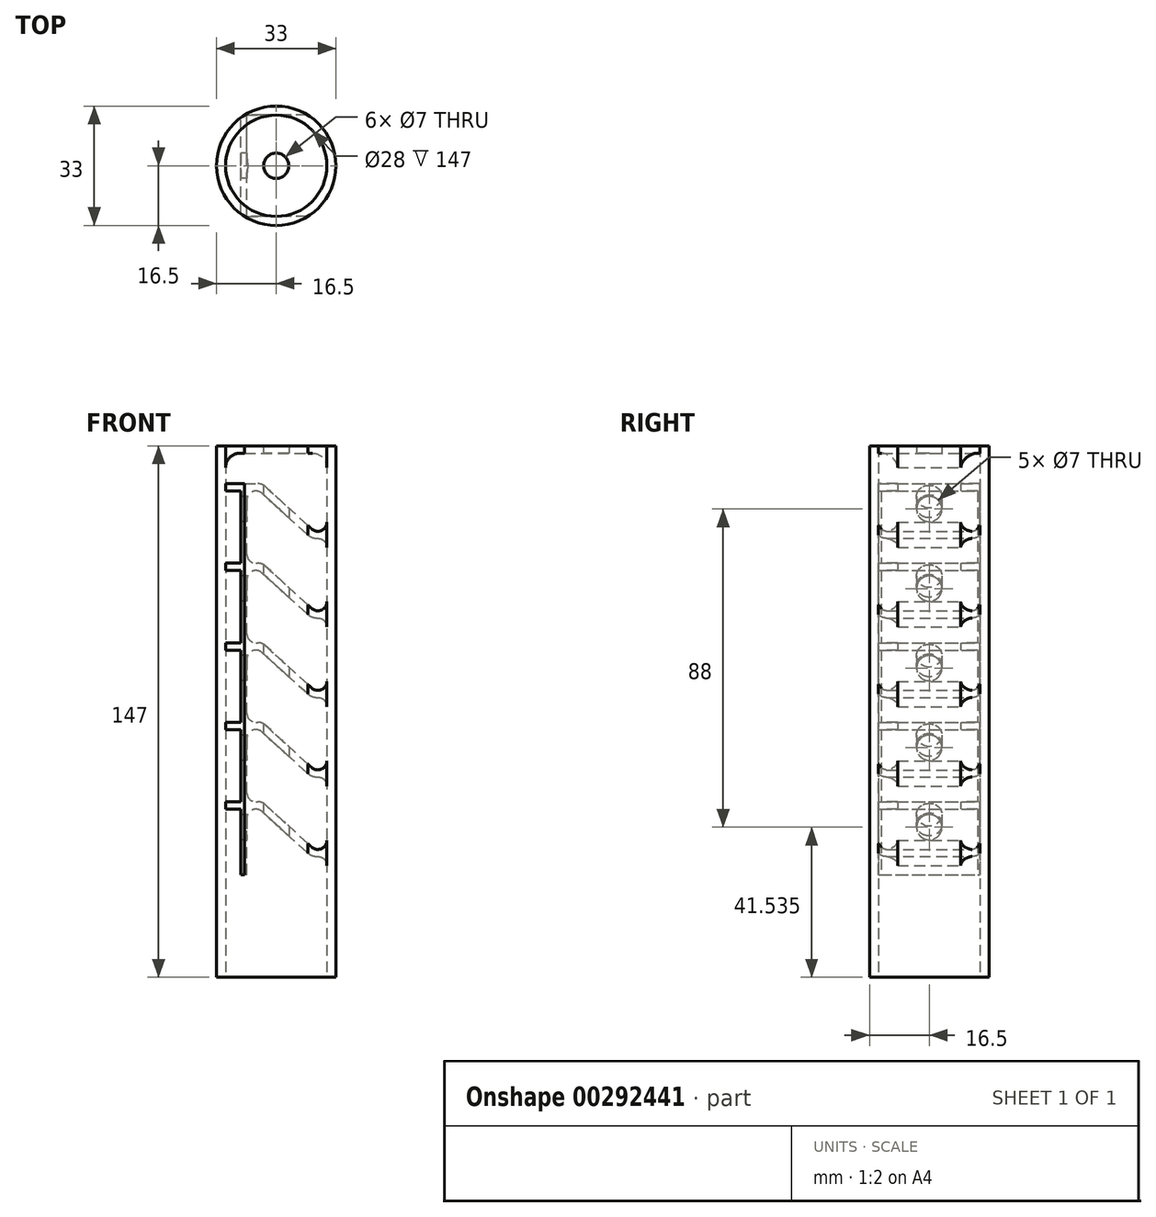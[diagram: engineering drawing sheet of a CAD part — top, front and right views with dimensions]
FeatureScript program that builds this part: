
annotation { "Feature Type Name" : "Feature", "Feature Type Description" : "" }
export const myFeature = defineFeature(function(context is Context, id is Id, definition is map)
    precondition{}
    {
        {
            var Q0;
            Q0=qCreatedBy(makeId("Front.planeOp"),FACE);
            var sketch = newSketch(context, id + "F0", { "sketchPlane" : qUnion([Q0])});
            skLineSegment(sketch, "E0.left", {"start": v(0, 0) * mm, "end": v(0, 125) * mm, "construction": true});
            skLineSegment(sketch, "E0.right", {"start": v(14, 0) * mm, "end": v(14, 125) * mm, "construction": true});
            skLineSegment(sketch, "E1.MirrorCS", {"start": v(-14, 0) * mm, "end": v(-14, 125) * mm, "construction": true});
            skLineSegment(sketch, "E2", {"start": v(-14, 125) * mm, "end": v(14, 125) * mm, "construction": true});
            skLineSegment(sketch, "E3", {"start": v(-3.5, 0) * mm, "end": v(-3.5, 125.09) * mm, "construction": true});
            skLineSegment(sketch, "E4", {"start": v(-9.71, 0) * mm, "end": v(-9.71, 34.88) * mm, "construction": true});
            skLineSegment(sketch, "E5", {"start": v(-3.5, 0) * mm, "end": v(-3.5, 73.23) * mm, "construction": true});
            skLineSegment(sketch, "E6.MirrorCS", {"start": v(3.5, 0) * mm, "end": v(3.5, 73.23) * mm, "construction": true});
            skLineSegment(sketch, "E7", {"start": v(-9.71, 36.85) * mm, "end": v(-9.71, 64.07) * mm, "construction": true});
            skCircle(sketch, "E8", {"center": v(11.5, 30.91) * mm, "radius": 2.5 * mm, "construction": true});
            skCircle(sketch, "E9", {"center": v(11.5, 37.89) * mm, "radius": 2.5 * mm, "construction": true});
            skCircle(sketch, "E10", {"center": v(-5.61, 44.03) * mm, "radius": 2.5 * mm, "construction": true});
            skCircle(sketch, "E11", {"center": v(-5.64, 51.03) * mm, "radius": 2.47 * mm, "construction": true});
            skLineSegment(sketch, "E12", {"start": v(-3.03, 47.77) * mm, "end": v(9.81, 36.04) * mm, "construction": true});
            skLineSegment(sketch, "E13", {"start": v(-4.64, 48.56) * mm, "end": v(-9.71, 48.56) * mm, "construction": true});
            skLineSegment(sketch, "E14", {"start": v(-5.61, 46.53) * mm, "end": v(-9.71, 46.53) * mm, "construction": true});
            skArc(sketch, "E15", {"start": v(14, 30.91) * mm, "mid": v(13.27, 32.68) * mm, "end": v(11.5, 33.41) * mm});
            skArc(sketch, "E16", {"start": v(14, 37.89) * mm, "mid": v(12.5, 35.6) * mm, "end": v(9.81, 36.04) * mm});
            skArc(sketch, "E17", {"start": v(-8.11, 51.03) * mm, "mid": v(-7.39, 49.28) * mm, "end": v(-5.64, 48.56) * mm});
            skArc(sketch, "E18", {"start": v(-8.11, 44.03) * mm, "mid": v(-6.62, 46.31) * mm, "end": v(-3.92, 45.87) * mm});
            skLineSegment(sketch, "E19", {"start": v(-9.71, 51.03) * mm, "end": v(-8.11, 51.03) * mm});
            skLineSegment(sketch, "E20", {"start": v(-14, 48.56) * mm, "end": v(-14, 46.53) * mm});
            skLineSegment(sketch, "E21", {"start": v(-14, 48.56) * mm, "end": v(-9.71, 48.56) * mm});
            skLineSegment(sketch, "E22", {"start": v(-9.71, 48.56) * mm, "end": v(-9.71, 51.03) * mm});
            skLineSegment(sketch, "E23", {"start": v(-14, 46.53) * mm, "end": v(-9.71, 46.53) * mm});
            skLineSegment(sketch, "E24", {"start": v(-8.11, 28.4) * mm, "end": v(-9.71, 28.41) * mm});
            skLineSegment(sketch, "E25", {"start": v(-5.64, 48.56) * mm, "end": v(-5.06, 48.56) * mm});
            skLineSegment(sketch, "E26", {"start": v(9.81, 36.04) * mm, "end": v(-3.9, 48.56) * mm});
            skLineSegment(sketch, "E27", {"start": v(14, 37.89) * mm, "end": v(14, 30.91) * mm});
            skLineSegment(sketch, "E28", {"start": v(-8.11, 28.4) * mm, "end": v(-8.11, 44.03) * mm});
            skLineSegment(sketch, "E29", {"start": v(-9.71, 46.53) * mm, "end": v(-9.71, 28.41) * mm});
            skPoint(sketch, "E30.visualSharp", {"position": v(-3.9, 48.56) * mm});
            skArc(sketch, "E30.filletArc", {"start": v(-3.03, 47.77) * mm, "mid": v(-3.97, 48.36) * mm, "end": v(-5.06, 48.56) * mm});
            skArc(sketch, "E31", {"start": v(11.5, 33.41) * mm, "mid": v(9.87, 33.72) * mm, "end": v(8.46, 34.6) * mm});
            skLineSegment(sketch, "E32", {"start": v(8.46, 34.6) * mm, "end": v(-3.92, 45.87) * mm});
            skLineSegment(sketch, "E33.0.1.0", {"start": v(-14, 70.56) * mm, "end": v(-9.71, 70.56) * mm});
            skLineSegment(sketch, "E33.0.1.1", {"start": v(-5.61, 68.53) * mm, "end": v(-9.71, 68.53) * mm, "construction": true});
            skLineSegment(sketch, "E33.0.1.2", {"start": v(-3.03, 69.77) * mm, "end": v(9.81, 58.04) * mm, "construction": true});
            skLineSegment(sketch, "E33.0.1.3", {"start": v(8.46, 56.6) * mm, "end": v(-3.92, 67.87) * mm});
            skLineSegment(sketch, "E33.0.1.4", {"start": v(-9.71, 68.53) * mm, "end": v(-9.71, 50.41) * mm});
            skPoint(sketch, "E33.0.1.5", {"position": v(-3.9, 70.56) * mm});
            skLineSegment(sketch, "E33.0.1.6", {"start": v(-8.11, 50.4) * mm, "end": v(-8.11, 66.03) * mm});
            skLineSegment(sketch, "E33.0.1.7", {"start": v(-4.64, 70.56) * mm, "end": v(-9.71, 70.56) * mm, "construction": true});
            skLineSegment(sketch, "E33.0.1.8", {"start": v(-14, 68.53) * mm, "end": v(-9.71, 68.53) * mm});
            skLineSegment(sketch, "E33.0.1.9", {"start": v(14, 59.89) * mm, "end": v(14, 52.91) * mm});
            skArc(sketch, "E33.0.1.10", {"start": v(-8.11, 66.03) * mm, "mid": v(-6.62, 68.31) * mm, "end": v(-3.92, 67.87) * mm});
            skLineSegment(sketch, "E33.0.1.11", {"start": v(9.81, 58.04) * mm, "end": v(-3.9, 70.56) * mm});
            skArc(sketch, "E33.0.1.12", {"start": v(14, 52.91) * mm, "mid": v(13.27, 54.68) * mm, "end": v(11.5, 55.41) * mm});
            skArc(sketch, "E33.0.1.13", {"start": v(14, 59.89) * mm, "mid": v(12.5, 57.6) * mm, "end": v(9.81, 58.04) * mm});
            skArc(sketch, "E33.0.1.14", {"start": v(-8.11, 73.03) * mm, "mid": v(-7.39, 71.28) * mm, "end": v(-5.64, 70.56) * mm});
            skArc(sketch, "E33.0.1.15", {"start": v(11.5, 55.41) * mm, "mid": v(9.87, 55.72) * mm, "end": v(8.46, 56.6) * mm});
            skLineSegment(sketch, "E33.0.1.16", {"start": v(-9.71, 70.56) * mm, "end": v(-9.71, 73.03) * mm});
            skLineSegment(sketch, "E33.0.1.17", {"start": v(-9.71, 73.03) * mm, "end": v(-8.11, 73.03) * mm});
            skLineSegment(sketch, "E33.0.1.18", {"start": v(-14, 70.56) * mm, "end": v(-14, 68.53) * mm});
            skLineSegment(sketch, "E33.0.1.19", {"start": v(-8.11, 50.4) * mm, "end": v(-9.71, 50.41) * mm});
            skArc(sketch, "E33.0.1.20", {"start": v(-3.03, 69.77) * mm, "mid": v(-3.97, 70.36) * mm, "end": v(-5.06, 70.56) * mm});
            skLineSegment(sketch, "E33.0.1.21", {"start": v(-5.64, 70.56) * mm, "end": v(-5.06, 70.56) * mm});
            skLineSegment(sketch, "E33.0.2.0", {"start": v(-14, 92.56) * mm, "end": v(-9.71, 92.56) * mm});
            skLineSegment(sketch, "E33.0.2.1", {"start": v(-5.61, 90.53) * mm, "end": v(-9.71, 90.53) * mm, "construction": true});
            skLineSegment(sketch, "E33.0.2.2", {"start": v(-3.03, 91.77) * mm, "end": v(9.81, 80.04) * mm, "construction": true});
            skLineSegment(sketch, "E33.0.2.3", {"start": v(8.46, 78.6) * mm, "end": v(-3.92, 89.87) * mm});
            skLineSegment(sketch, "E33.0.2.4", {"start": v(-9.71, 90.53) * mm, "end": v(-9.71, 72.41) * mm});
            skPoint(sketch, "E33.0.2.5", {"position": v(-3.9, 92.56) * mm});
            skLineSegment(sketch, "E33.0.2.6", {"start": v(-8.11, 72.4) * mm, "end": v(-8.11, 88.03) * mm});
            skLineSegment(sketch, "E33.0.2.7", {"start": v(-4.64, 92.56) * mm, "end": v(-9.71, 92.56) * mm, "construction": true});
            skLineSegment(sketch, "E33.0.2.8", {"start": v(-14, 90.53) * mm, "end": v(-9.71, 90.53) * mm});
            skLineSegment(sketch, "E33.0.2.9", {"start": v(14, 81.89) * mm, "end": v(14, 74.91) * mm});
            skArc(sketch, "E33.0.2.10", {"start": v(-8.11, 88.03) * mm, "mid": v(-6.62, 90.31) * mm, "end": v(-3.92, 89.87) * mm});
            skLineSegment(sketch, "E33.0.2.11", {"start": v(9.81, 80.04) * mm, "end": v(-3.9, 92.56) * mm});
            skArc(sketch, "E33.0.2.12", {"start": v(14, 74.91) * mm, "mid": v(13.27, 76.68) * mm, "end": v(11.5, 77.41) * mm});
            skArc(sketch, "E33.0.2.13", {"start": v(14, 81.89) * mm, "mid": v(12.5, 79.6) * mm, "end": v(9.81, 80.04) * mm});
            skArc(sketch, "E33.0.2.14", {"start": v(-8.11, 95.03) * mm, "mid": v(-7.39, 93.28) * mm, "end": v(-5.64, 92.56) * mm});
            skArc(sketch, "E33.0.2.15", {"start": v(11.5, 77.41) * mm, "mid": v(9.87, 77.72) * mm, "end": v(8.46, 78.6) * mm});
            skLineSegment(sketch, "E33.0.2.16", {"start": v(-9.71, 92.56) * mm, "end": v(-9.71, 95.03) * mm});
            skLineSegment(sketch, "E33.0.2.17", {"start": v(-9.71, 95.03) * mm, "end": v(-8.11, 95.03) * mm});
            skLineSegment(sketch, "E33.0.2.18", {"start": v(-14, 92.56) * mm, "end": v(-14, 90.53) * mm});
            skLineSegment(sketch, "E33.0.2.19", {"start": v(-8.11, 72.4) * mm, "end": v(-9.71, 72.41) * mm});
            skArc(sketch, "E33.0.2.20", {"start": v(-3.03, 91.77) * mm, "mid": v(-3.97, 92.36) * mm, "end": v(-5.06, 92.56) * mm});
            skLineSegment(sketch, "E33.0.2.21", {"start": v(-5.64, 92.56) * mm, "end": v(-5.06, 92.56) * mm});
            skLineSegment(sketch, "E33.0.3.0", {"start": v(-14, 114.56) * mm, "end": v(-9.71, 114.56) * mm});
            skLineSegment(sketch, "E33.0.3.1", {"start": v(-5.61, 112.53) * mm, "end": v(-9.71, 112.53) * mm, "construction": true});
            skLineSegment(sketch, "E33.0.3.2", {"start": v(-3.03, 113.77) * mm, "end": v(9.81, 102.04) * mm, "construction": true});
            skLineSegment(sketch, "E33.0.3.3", {"start": v(8.46, 100.6) * mm, "end": v(-3.92, 111.87) * mm});
            skLineSegment(sketch, "E33.0.3.4", {"start": v(-9.71, 112.53) * mm, "end": v(-9.71, 94.41) * mm});
            skPoint(sketch, "E33.0.3.5", {"position": v(-3.9, 114.56) * mm});
            skLineSegment(sketch, "E33.0.3.6", {"start": v(-8.11, 94.4) * mm, "end": v(-8.11, 110.03) * mm});
            skLineSegment(sketch, "E33.0.3.7", {"start": v(-4.64, 114.56) * mm, "end": v(-9.71, 114.56) * mm, "construction": true});
            skLineSegment(sketch, "E33.0.3.8", {"start": v(-14, 112.53) * mm, "end": v(-9.71, 112.53) * mm});
            skLineSegment(sketch, "E33.0.3.9", {"start": v(14, 103.89) * mm, "end": v(14, 96.91) * mm});
            skArc(sketch, "E33.0.3.10", {"start": v(-8.11, 110.03) * mm, "mid": v(-6.62, 112.31) * mm, "end": v(-3.92, 111.87) * mm});
            skLineSegment(sketch, "E33.0.3.11", {"start": v(9.81, 102.04) * mm, "end": v(-3.9, 114.56) * mm});
            skArc(sketch, "E33.0.3.12", {"start": v(14, 96.91) * mm, "mid": v(13.27, 98.68) * mm, "end": v(11.5, 99.41) * mm});
            skArc(sketch, "E33.0.3.13", {"start": v(14, 103.89) * mm, "mid": v(12.5, 101.6) * mm, "end": v(9.81, 102.04) * mm});
            skArc(sketch, "E33.0.3.14", {"start": v(-8.11, 117.03) * mm, "mid": v(-7.39, 115.28) * mm, "end": v(-5.64, 114.56) * mm});
            skArc(sketch, "E33.0.3.15", {"start": v(11.5, 99.41) * mm, "mid": v(9.87, 99.72) * mm, "end": v(8.46, 100.6) * mm});
            skLineSegment(sketch, "E33.0.3.16", {"start": v(-9.71, 114.56) * mm, "end": v(-9.71, 117.03) * mm});
            skLineSegment(sketch, "E33.0.3.17", {"start": v(-9.71, 117.03) * mm, "end": v(-8.11, 117.03) * mm});
            skLineSegment(sketch, "E33.0.3.18", {"start": v(-14, 114.56) * mm, "end": v(-14, 112.53) * mm});
            skLineSegment(sketch, "E33.0.3.19", {"start": v(-8.11, 94.4) * mm, "end": v(-9.71, 94.41) * mm});
            skArc(sketch, "E33.0.3.20", {"start": v(-3.03, 113.77) * mm, "mid": v(-3.97, 114.36) * mm, "end": v(-5.06, 114.56) * mm});
            skLineSegment(sketch, "E33.0.3.21", {"start": v(-5.64, 114.56) * mm, "end": v(-5.06, 114.56) * mm});
            skLineSegment(sketch, "E33.0.4.0", {"start": v(-14, 136.56) * mm, "end": v(-9.71, 136.56) * mm});
            skLineSegment(sketch, "E33.0.4.1", {"start": v(-5.61, 134.53) * mm, "end": v(-9.71, 134.53) * mm, "construction": true});
            skLineSegment(sketch, "E33.0.4.2", {"start": v(-3.03, 135.77) * mm, "end": v(9.81, 124.04) * mm, "construction": true});
            skLineSegment(sketch, "E33.0.4.3", {"start": v(8.46, 122.6) * mm, "end": v(-3.92, 133.87) * mm});
            skLineSegment(sketch, "E33.0.4.4", {"start": v(-9.71, 134.53) * mm, "end": v(-9.71, 116.41) * mm});
            skPoint(sketch, "E33.0.4.5", {"position": v(-3.9, 136.56) * mm});
            skLineSegment(sketch, "E33.0.4.6", {"start": v(-8.11, 116.4) * mm, "end": v(-8.11, 132.03) * mm});
            skLineSegment(sketch, "E33.0.4.7", {"start": v(-4.64, 136.56) * mm, "end": v(-9.71, 136.56) * mm, "construction": true});
            skLineSegment(sketch, "E33.0.4.8", {"start": v(-14, 134.53) * mm, "end": v(-9.71, 134.53) * mm});
            skLineSegment(sketch, "E33.0.4.9", {"start": v(14, 125.89) * mm, "end": v(14, 118.91) * mm});
            skArc(sketch, "E33.0.4.10", {"start": v(-8.11, 132.03) * mm, "mid": v(-6.62, 134.31) * mm, "end": v(-3.92, 133.87) * mm});
            skLineSegment(sketch, "E33.0.4.11", {"start": v(9.81, 124.04) * mm, "end": v(-3.9, 136.56) * mm});
            skArc(sketch, "E33.0.4.12", {"start": v(14, 118.91) * mm, "mid": v(13.27, 120.68) * mm, "end": v(11.5, 121.41) * mm});
            skArc(sketch, "E33.0.4.13", {"start": v(14, 125.89) * mm, "mid": v(12.5, 123.6) * mm, "end": v(9.81, 124.04) * mm});
            skArc(sketch, "E33.0.4.15", {"start": v(11.5, 121.41) * mm, "mid": v(9.87, 121.72) * mm, "end": v(8.46, 122.6) * mm});
            skLineSegment(sketch, "E33.0.4.18", {"start": v(-14, 136.56) * mm, "end": v(-14, 134.53) * mm});
            skLineSegment(sketch, "E33.0.4.19", {"start": v(-8.11, 116.4) * mm, "end": v(-9.71, 116.41) * mm});
            skArc(sketch, "E33.0.4.20", {"start": v(-3.03, 135.77) * mm, "mid": v(-3.97, 136.36) * mm, "end": v(-5.06, 136.56) * mm});
            skLineSegment(sketch, "E33.0.4.21", {"start": v(-5.64, 136.56) * mm, "end": v(-5.06, 136.56) * mm});
            skLineSegment(sketch, "E33.direction1", {"start": v(-9.71, 28.41) * mm, "end": v(15.29, 28.41) * mm, "construction": true});
            skLineSegment(sketch, "E33.direction2", {"start": v(-9.71, 28.41) * mm, "end": v(-9.71, 50.41) * mm, "construction": true});
            skLineSegment(sketch, "E34", {"start": v(14, 125.89) * mm, "end": v(14, 144.66) * mm, "construction": true});
            skLineSegment(sketch, "E35", {"start": v(-14, 125) * mm, "end": v(-14, 144.67) * mm, "construction": true});
            skLineSegment(sketch, "E36", {"start": v(-14.85, 147) * mm, "end": v(15.2, 147) * mm, "construction": true});
            skLineSegment(sketch, "E37", {"start": v(-14.85, 145) * mm, "end": v(17.03, 145) * mm, "construction": true});
            skCircle(sketch, "E38", {"center": v(-10, 141) * mm, "radius": 4 * mm, "construction": true});
            skCircle(sketch, "E39", {"center": v(10, 141) * mm, "radius": 4 * mm, "construction": true});
            skArc(sketch, "E40", {"start": v(-14, 141) * mm, "mid": v(-12.83, 143.82) * mm, "end": v(-10, 145) * mm});
            skArc(sketch, "E41", {"start": v(14, 141) * mm, "mid": v(12.83, 143.82) * mm, "end": v(10, 145) * mm});
            skLineSegment(sketch, "E42", {"start": v(-10, 145) * mm, "end": v(10, 145) * mm});
            skLineSegment(sketch, "E43", {"start": v(14, 141) * mm, "end": v(14, 147) * mm});
            skLineSegment(sketch, "E44", {"start": v(14, 147) * mm, "end": v(-14, 147) * mm});
            skLineSegment(sketch, "E45", {"start": v(-14, 147) * mm, "end": v(-14, 141) * mm});
            skLineSegment(sketch, "E46", {"start": v(-9.71, 136.56) * mm, "end": v(-5.64, 136.56) * mm});
            skSolve(sketch);
        }
        {
            var Q0;
            Q0 = qSketchRegion(id + "F0", true);
            extrude(context, id + "F1", {"entities" : qUnion([Q0]), "depth" : 14 * mm, "hasSecondDirection" : true, "secondDirectionOppositeDirection" : true, "secondDirectionDepth" : 14 * mm});
        }
        {
            var Q0;
            Q0=makeQuery(id+"F1.opExtrude","SWEPT_FACE",FACE,{"disambiguationData":[OSD([sQuery(id+"F0.wireOp",EDGE,"E29")])]});
            var sketch = newSketch(context, id + "F2", { "sketchPlane" : qUnion([Q0])});
            skCircle(sketch, "E47", {"center": v(0, 41.53) * mm, "radius": 3.5 * mm});
            skCircle(sketch, "E48.0.1.0", {"center": v(0, 63.53) * mm, "radius": 3.5 * mm});
            skCircle(sketch, "E48.0.2.0", {"center": v(0, 85.53) * mm, "radius": 3.5 * mm});
            skCircle(sketch, "E48.0.3.0", {"center": v(0, 107.53) * mm, "radius": 3.5 * mm});
            skCircle(sketch, "E48.0.4.0", {"center": v(0, 129.53) * mm, "radius": 3.5 * mm});
            skLineSegment(sketch, "E48.direction1", {"start": v(0, 41.53) * mm, "end": v(25, 41.53) * mm, "construction": true});
            skLineSegment(sketch, "E48.direction2", {"start": v(0, 41.53) * mm, "end": v(0, 63.53) * mm, "construction": true});
            skSolve(sketch);
        }
        {
            var Q0;
            Q0 = qSketchRegion(id + "F2", true);
            extrude(context, id + "F3", {"entities" : qUnion([Q0]), "operationType" : NewBodyOperationType.REMOVE, "oppositeDirection" : true, "depth" : 5 * mm});
        }
        {
            var Q0;
            Q0=qCreatedBy(makeId("Top.planeOp"),FACE);
            var sketch = newSketch(context, id + "F4", { "sketchPlane" : qUnion([Q0])});
            skCircle(sketch, "E49", {"center": v(0, 0) * mm, "radius": 14 * mm});
            skCircle(sketch, "E50", {"center": v(0, 0) * mm, "radius": 16.5 * mm});
            skSolve(sketch);
        }
        {
            var Q0;
            Q0 = qSketchRegion(id + "F4", true);
            extrude(context, id + "F5", {"entities" : qUnion([Q0]), "depth" : 147 * mm});
        }
        {
            var Q0;
            Q0=makeQuery(id+"F5.opExtrude","CAP_FACE",FACE,{"disambiguationData":[OSD([sQuery(id+"F4.wireOp",EDGE,"E49"),sQuery(id+"F4.wireOp",EDGE,"E50")])],"isStart":true});
            var sketch = newSketch(context, id + "F6", { "sketchPlane" : qUnion([Q0])});
            skCircle(sketch, "E51.0", {"center": v(0, 0) * mm, "radius": 16.5 * mm});
            skCircle(sketch, "E52", {"center": v(0, 0) * mm, "radius": 19.98 * mm});
            skSolve(sketch);
        }
        {
            var Q0;
            Q0 = qSketchRegion(id + "F6", true);
            extrude(context, id + "F7", {"entities" : qUnion([Q0]), "operationType" : NewBodyOperationType.REMOVE, "oppositeDirection" : true, "depth" : 147.4 * mm});
        }
        {
            var Q0;
            Q0=makeQuery(id+"F5.opExtrude","CAP_FACE",FACE,{"disambiguationData":[OSD([sQuery(id+"F4.wireOp",EDGE,"E49"),sQuery(id+"F4.wireOp",EDGE,"E50")])],"isStart":true});
            var sketch = newSketch(context, id + "F8", { "sketchPlane" : qUnion([Q0])});
            skCircle(sketch, "E53", {"center": v(0, 0) * mm, "radius": 3.5 * mm});
            skSolve(sketch);
        }
        {
            var Q0;
            Q0 = qSketchRegion(id + "F8", true);
            extrude(context, id + "F9", {"entities" : qUnion([Q0]), "operationType" : NewBodyOperationType.REMOVE, "oppositeDirection" : true, "depth" : 148.1 * mm});
        }
        {
            var Q0;
            Q0=makeQuery(id+"F1.opExtrude","SWEPT_FACE",FACE,{"disambiguationData":[OSD([sQuery(id+"F0.wireOp",EDGE,"E44")])]});
            var sketch = newSketch(context, id + "F10", { "sketchPlane" : qUnion([Q0])});
            skCircle(sketch, "E54", {"center": v(0, 0) * mm, "radius": 3 * mm});
            skSolve(sketch);
        }
        {
            var Q0;
            Q0 = qSketchRegion(id + "F10", true);
            extrude(context, id + "F11", {"entities" : qUnion([Q0]), "operationType" : NewBodyOperationType.REMOVE, "oppositeDirection" : true, "depth" : 5 * mm});
        }
    });
